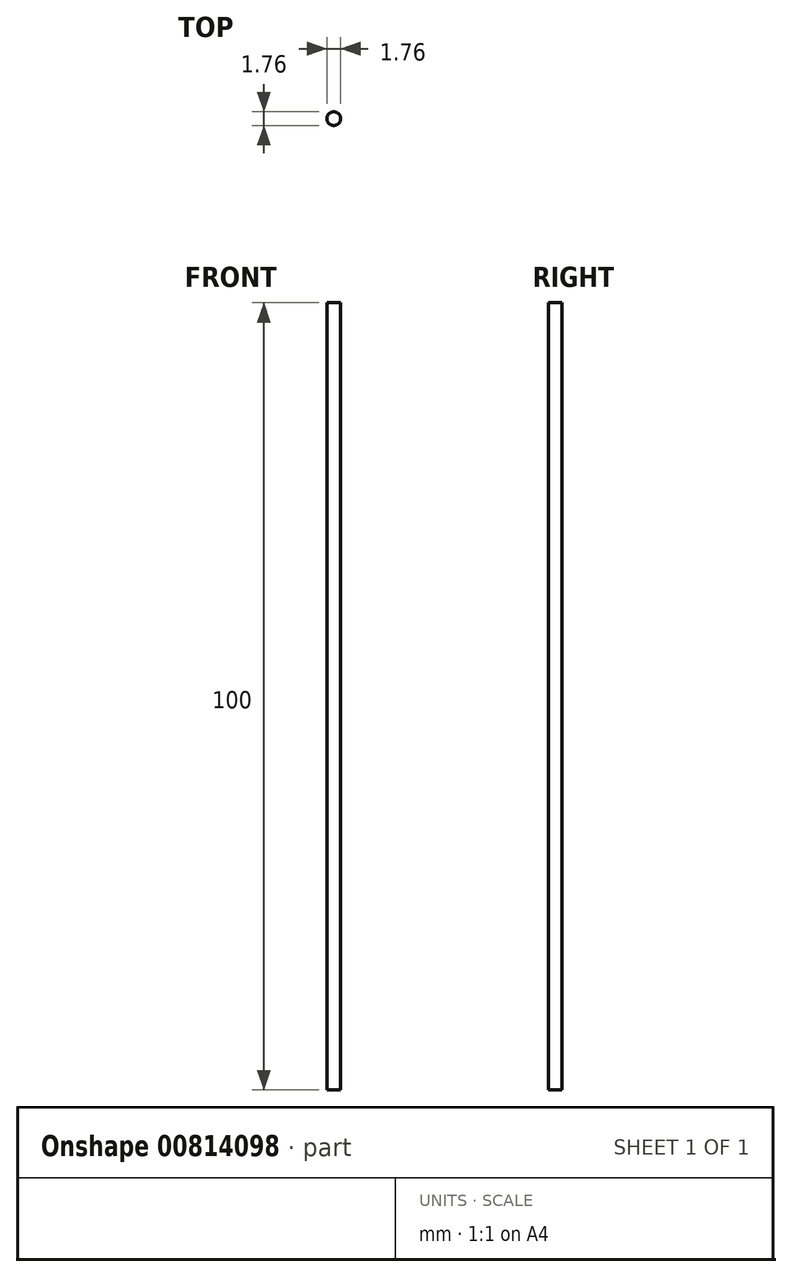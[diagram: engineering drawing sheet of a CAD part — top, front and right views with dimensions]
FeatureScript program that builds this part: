
annotation { "Feature Type Name" : "Feature", "Feature Type Description" : "" }
export const myFeature = defineFeature(function(context is Context, id is Id, definition is map)
    precondition{}
    {
        {
            var Q0;
            Q0=qCreatedBy(makeId("Top.planeOp"),FACE);
            var sketch = newSketch(context, id + "F0", { "sketchPlane" : qUnion([Q0])});
            skCircle(sketch, "E0", {"center": v(0, 0) * mm, "radius": 0.88 * mm});
            skSolve(sketch);
        }
        {
            var Q0;
            Q0 = qSketchRegion(id + "F0", true);
            extrude(context, id + "F1", {"entities" : qUnion([Q0]), "depth" : 100 * mm, "offsetDistance" : 25 * mm});
        }
    });
